# Revit family: VENTS-VKV
name_source: partatom
category: Mechanical Equipment
units: mm (PartAtom-declared; Revit-internal decimal feet)

## family parameters
Always vertical = Yes
Classification = None
Cut with Voids When Loaded = No
OmniClass Number = 23.75.35.17.14
OmniClass Title = Fans, Single Units
Part Type = Normal
Room Calculation Point = No
Round Connector Dimension = Use Diameter
Shared = No
Work Plane-Based = No

## types (38) — shared parameters
Casing Material = Fan Zinc
DboxFixDepth = 2 mm  [stored 0.00656168 ft]
DboxFixW = 80 mm  [stored 0.262467 ft]
Description = Centrifugal roof fan with vertical air discharge
Family Version = 1.0
Grid Material = Cover Grid Cross
Load Classification = HVAC
Maintenance Zone Front Depth = 400 mm
Maintenance Zone Material = Maintenance Zone
Maintenance Zone Side Depth = 400 mm
Manufacturer = Vents
Power Factor = 1
Protection rating = IP X4
URL = https://ventilation-system.com
zero-valued in all types: Sound Pressure Level at 1 m (dBA), Sound Pressure Level at 3 m (dBA)

## per-type parameters (varying)
- VKV 2E 190 (50Hz): A=417 mm; Af=155 mm; AswBottom=320 mm; B=355 mm; C=245 mm  [stored 0.803806 ft]; Current=0 A; D=213 mm  [stored 0.698819 ft]; DboxFixBottomH=40 mm  [stored 0.131234 ft]; DboxFixH=112 mm  [stored 0.367454 ft]; Duct Connection Size=180 mm  [stored 0.590551 ft]; H=170 mm  [stored 0.557743 ft]; Hb=36 mm  [stored 0.11811 ft]; Hc=82 mm  [stored 0.269029 ft]; Ht=52 mm  [stored 0.170604 ft]; L=480 mm; Maximum Air Flow=610 m³/h; Model=VKV 2E 190; Noise Level at 3 m (dBa)=48; Number of Poles=1; RPM (min-1)=2680; Transported Air Temperature (°C)=-25...+50; Type Comments=Centrifugal roof fan VKV 2E 190; Voltage=230 V; Weight=7.00 kg; gsA=334 mm
- VKV 2E 190 (60Hz): A=417 mm; Af=155 mm; AswBottom=320 mm; B=355 mm; C=245 mm  [stored 0.803806 ft]; Current=0 A; D=213 mm  [stored 0.698819 ft]; DboxFixBottomH=40 mm  [stored 0.131234 ft]; DboxFixH=112 mm  [stored 0.367454 ft]; Duct Connection Size=180 mm  [stored 0.590551 ft]; H=170 mm  [stored 0.557743 ft]; Hb=36 mm  [stored 0.11811 ft]; Hc=82 mm  [stored 0.269029 ft]; Ht=52 mm  [stored 0.170604 ft]; L=480 mm; Maximum Air Flow=654 m³/h; Model=VKV 2E 190; Noise Level at 3 m (dBa)=49; Number of Poles=1; RPM (min-1)=2980; Transported Air Temperature (°C)=-25...+50; Type Comments=Centrifugal roof fan VKV 2E 190; Voltage=230 V; Weight=7.00 kg; gsA=334 mm
- VKV 2E 220 (50Hz): A=417 mm; Af=155 mm; AswBottom=320 mm; B=355 mm; C=245 mm  [stored 0.803806 ft]; Current=0 A; D=213 mm  [stored 0.698819 ft]; DboxFixBottomH=40 mm  [stored 0.131234 ft]; DboxFixH=122 mm  [stored 0.400262 ft]; Duct Connection Size=180 mm  [stored 0.590551 ft]; H=190 mm; Hb=31 mm  [stored 0.101706 ft]; Hc=131 mm; Ht=28 mm  [stored 0.0918635 ft]; L=480 mm; Maximum Air Flow=880 m³/h; Model=VKV 2E 220; Noise Level at 3 m (dBa)=50; Number of Poles=1; RPM (min-1)=2580; Transported Air Temperature (°C)=-25...+50; Type Comments=Centrifugal roof fan VKV 2E 220; Voltage=230 V; Weight=7.00 kg; gsA=334 mm
- VKV 2E 220 (60Hz): A=417 mm; Af=155 mm; AswBottom=320 mm; B=355 mm; C=245 mm  [stored 0.803806 ft]; Current=1 A; D=213 mm  [stored 0.698819 ft]; DboxFixBottomH=40 mm  [stored 0.131234 ft]; DboxFixH=122 mm  [stored 0.400262 ft]; Duct Connection Size=180 mm  [stored 0.590551 ft]; H=190 mm; Hb=31 mm  [stored 0.101706 ft]; Hc=131 mm; Ht=28 mm  [stored 0.0918635 ft]; L=480 mm; Maximum Air Flow=883 m³/h; Model=VKV 2E 220; Noise Level at 3 m (dBa)=51; Number of Poles=1; RPM (min-1)=2840; Transported Air Temperature (°C)=-25...+50; Type Comments=Centrifugal roof fan VKV 2E 220; Voltage=230 V; Weight=7.00 kg; gsA=334 mm
- VKV 2E 225 (50Hz): A=417 mm; Af=155 mm; AswBottom=320 mm; B=355 mm; C=245 mm  [stored 0.803806 ft]; Current=1 A; D=210 mm  [stored 0.688976 ft]; DboxFixBottomH=40 mm  [stored 0.131234 ft]; DboxFixH=122 mm  [stored 0.400262 ft]; Duct Connection Size=180 mm  [stored 0.590551 ft]; H=215 mm; Hb=31 mm  [stored 0.101706 ft]; Hc=136 mm; Ht=48 mm  [stored 0.15748 ft]; L=480 mm; Maximum Air Flow=915 m³/h; Model=VKV 2E 225; Noise Level at 3 m (dBa)=51; Number of Poles=1; RPM (min-1)=2790; Transported Air Temperature (°C)=-25...+50; Type Comments=Centrifugal roof fan VKV 2E 225; Voltage=230 V; Weight=7.00 kg; gsA=334 mm
- VKV 2E 225 (60Hz): A=417 mm; Af=155 mm; AswBottom=320 mm; B=355 mm; C=245 mm  [stored 0.803806 ft]; Current=1 A; D=210 mm  [stored 0.688976 ft]; DboxFixBottomH=40 mm  [stored 0.131234 ft]; DboxFixH=122 mm  [stored 0.400262 ft]; Duct Connection Size=180 mm  [stored 0.590551 ft]; H=215 mm; Hb=31 mm  [stored 0.101706 ft]; Hc=136 mm; Ht=48 mm  [stored 0.15748 ft]; L=480 mm; Maximum Air Flow=1010 m³/h; Model=VKV 2E 225; Noise Level at 3 m (dBa)=52; Number of Poles=1; RPM (min-1)=2820; Transported Air Temperature (°C)=-25...+50; Type Comments=Centrifugal roof fan VKV 2E 225; Voltage=230 V; Weight=7.00 kg; gsA=334 mm
- VKV 4E 225 (50Hz): A=417 mm; Af=155 mm; AswBottom=320 mm; B=355 mm; C=245 mm  [stored 0.803806 ft]; Current=0 A; D=210 mm  [stored 0.688976 ft]; DboxFixBottomH=40 mm  [stored 0.131234 ft]; DboxFixH=122 mm  [stored 0.400262 ft]; Duct Connection Size=180 mm  [stored 0.590551 ft]; H=215 mm; Hb=31 mm  [stored 0.101706 ft]; Hc=136 mm; Ht=48 mm  [stored 0.15748 ft]; L=480 mm; Maximum Air Flow=738 m³/h; Model=VKV 4E 225; Noise Level at 3 m (dBa)=45; Number of Poles=1; RPM (min-1)=1400; Transported Air Temperature (°C)=-25...+50; Type Comments=Centrifugal roof fan VKV 4E 225; Voltage=230 V; Weight=7.00 kg; gsA=334 mm
- VKV 2E 250 (50Hz): A=481 mm; Af=179 mm; AswBottom=358 mm; B=425 mm; C=330 mm; Current=1 A; D=285 mm; DboxFixBottomH=36 mm  [stored 0.11811 ft]; DboxFixH=151 mm  [stored 0.495407 ft]; Duct Connection Size=250 mm; H=240 mm  [stored 0.787402 ft]; Hb=31 mm  [stored 0.101706 ft]; Hc=158 mm  [stored 0.518373 ft]; Ht=51 mm  [stored 0.167323 ft]; L=540 mm; Maximum Air Flow=1450 m³/h; Model=VKV 2E 250; Noise Level at 3 m (dBa)=54; Number of Poles=1; RPM (min-1)=2480; Transported Air Temperature (°C)=-25...+50; Type Comments=Centrifugal roof fan VKV 2E 250; Voltage=230 V; Weight=9.00 kg; gsA=385 mm
- VKV 2E 250 (60Hz): A=481 mm; Af=179 mm; AswBottom=358 mm; B=425 mm; C=330 mm; Current=1 A; D=285 mm; DboxFixBottomH=36 mm  [stored 0.11811 ft]; DboxFixH=151 mm  [stored 0.495407 ft]; Duct Connection Size=250 mm; H=240 mm  [stored 0.787402 ft]; Hb=31 mm  [stored 0.101706 ft]; Hc=158 mm  [stored 0.518373 ft]; Ht=51 mm  [stored 0.167323 ft]; L=540 mm; Maximum Air Flow=1320 m³/h; Model=VKV 2E 250; Noise Level at 3 m (dBa)=53; Number of Poles=1; RPM (min-1)=2320; Transported Air Temperature (°C)=-25...+50; Type Comments=Centrifugal roof fan VKV 2E 250; Voltage=230 V; Weight=9.00 kg; gsA=385 mm
- VKV 4E 250 (50Hz): A=481 mm; Af=179 mm; AswBottom=358 mm; B=425 mm; C=330 mm; Current=0 A; D=285 mm; DboxFixBottomH=36 mm  [stored 0.11811 ft]; DboxFixH=151 mm  [stored 0.495407 ft]; Duct Connection Size=250 mm; H=240 mm  [stored 0.787402 ft]; Hb=31 mm  [stored 0.101706 ft]; Hc=158 mm  [stored 0.518373 ft]; Ht=51 mm  [stored 0.167323 ft]; L=540 mm; Maximum Air Flow=820 m³/h; Model=VKV 4E 250; Noise Level at 3 m (dBa)=46; Number of Poles=1; RPM (min-1)=1440; Transported Air Temperature (°C)=-25...+50; Type Comments=Centrifugal roof fan VKV 4E 250; Voltage=230 V; Weight=9.00 kg; gsA=385 mm
- VKV 4E 280 (50Hz): A=547 mm; Af=204 mm; AswBottom=395 mm; B=425 mm; C=330 mm; Current=1 A; D=291 mm; DboxFixBottomH=53 mm  [stored 0.173885 ft]; DboxFixH=151 mm  [stored 0.495407 ft]; Duct Connection Size=250 mm; H=276 mm; Hb=31 mm  [stored 0.101706 ft]; Hc=194 mm  [stored 0.636483 ft]; Ht=51 mm  [stored 0.167323 ft]; L=600 mm; Maximum Air Flow=1490 m³/h; Model=VKV 4E 280; Noise Level at 3 m (dBa)=46; Number of Poles=1; RPM (min-1)=1446; Transported Air Temperature (°C)=-25...+50; Type Comments=Centrifugal roof fan VKV 4E 280; Voltage=230 V; Weight=13.00 kg; gsA=438 mm
- VKV 4E 280 (60Hz): A=547 mm; Af=204 mm; AswBottom=395 mm; B=425 mm; C=330 mm; Current=1 A; D=291 mm; DboxFixBottomH=53 mm  [stored 0.173885 ft]; DboxFixH=151 mm  [stored 0.495407 ft]; Duct Connection Size=250 mm; H=276 mm; Hb=31 mm  [stored 0.101706 ft]; Hc=194 mm  [stored 0.636483 ft]; Ht=51 mm  [stored 0.167323 ft]; L=600 mm; Maximum Air Flow=1520 m³/h; Model=VKV 4E 280; Noise Level at 3 m (dBa)=46; Number of Poles=1; RPM (min-1)=1710; Transported Air Temperature (°C)=-25...+50; Type Comments=Centrifugal roof fan VKV 4E 280; Voltage=230 V; Weight=13.00 kg; gsA=438 mm
- VKV 2E 310 (50Hz): A=613 mm; Af=229 mm; AswBottom=445 mm; B=477 mm; C=330 mm; Current=1 A; D=285 mm; DboxFixBottomH=75 mm; DboxFixH=151 mm  [stored 0.495407 ft]; Duct Connection Size=250 mm; H=300 mm; Hb=31 mm  [stored 0.101706 ft]; Hc=218 mm  [stored 0.715223 ft]; Ht=51 mm  [stored 0.167323 ft]; L=670 mm; Maximum Air Flow=2150 m³/h; Model=VKV 2E 310; Noise Level at 3 m (dBa)=58; Number of Poles=1; RPM (min-1)=2620; Transported Air Temperature (°C)=-25...+50; Type Comments=Centrifugal roof fan VKV 2E 310; Voltage=230 V; Weight=13.00 kg; gsA=490 mm
- VKV 4E 310 (50Hz): A=613 mm; Af=229 mm; AswBottom=445 mm; B=477 mm; C=330 mm; Current=1 A; D=285 mm; DboxFixBottomH=75 mm; DboxFixH=151 mm  [stored 0.495407 ft]; Duct Connection Size=250 mm; H=300 mm; Hb=31 mm  [stored 0.101706 ft]; Hc=218 mm  [stored 0.715223 ft]; Ht=51 mm  [stored 0.167323 ft]; L=670 mm; Maximum Air Flow=2265 m³/h; Model=VKV 4E 310; Noise Level at 3 m (dBa)=47; Number of Poles=1; RPM (min-1)=1420; Transported Air Temperature (°C)=-25...+50; Type Comments=Centrifugal roof fan VKV 4E 310; Voltage=230 V; Weight=20.00 kg; gsA=490 mm
- VKV 4E 310 (60Hz): A=613 mm; Af=229 mm; AswBottom=445 mm; B=477 mm; C=330 mm; Current=1 A; D=285 mm; DboxFixBottomH=75 mm; DboxFixH=151 mm  [stored 0.495407 ft]; Duct Connection Size=250 mm; H=300 mm; Hb=31 mm  [stored 0.101706 ft]; Hc=218 mm  [stored 0.715223 ft]; Ht=51 mm  [stored 0.167323 ft]; L=670 mm; Maximum Air Flow=2425 m³/h; Model=VKV 4E 310; Noise Level at 3 m (dBa)=49; Number of Poles=1; RPM (min-1)=1740; Transported Air Temperature (°C)=-25...+50; Type Comments=Centrifugal roof fan VKV 4E 310; Voltage=230 V; Weight=20.00 kg; gsA=490 mm
- VKV 4D 310 (50Hz): A=613 mm; Af=229 mm; AswBottom=445 mm; B=477 mm; C=750 mm; Current=0 A; D=285 mm; DboxFixBottomH=75 mm; DboxFixH=151 mm  [stored 0.495407 ft]; Duct Connection Size=250 mm; H=300 mm; Hb=31 mm  [stored 0.101706 ft]; Hc=218 mm  [stored 0.715223 ft]; Ht=51 mm  [stored 0.167323 ft]; L=670 mm; Maximum Air Flow=2300 m³/h; Model=VKV 4D 310; Noise Level at 3 m (dBa)=47; Number of Poles=3; RPM (min-1)=1410; Transported Air Temperature (°C)=-25...+50; Type Comments=Centrifugal roof fan VKV 4D 310; Voltage=400 V; Weight=19.00 kg; gsA=490 mm
- VKV 4D 310 (60Hz): A=613 mm; Af=229 mm; AswBottom=445 mm; B=477 mm; C=750 mm; Current=0 A; D=285 mm; DboxFixBottomH=75 mm; DboxFixH=151 mm  [stored 0.495407 ft]; Duct Connection Size=250 mm; H=300 mm; Hb=31 mm  [stored 0.101706 ft]; Hc=218 mm  [stored 0.715223 ft]; Ht=51 mm  [stored 0.167323 ft]; L=670 mm; Maximum Air Flow=2442 m³/h; Model=VKV 4D 310; Noise Level at 3 m (dBa)=48; Number of Poles=3; RPM (min-1)=1550; Transported Air Temperature (°C)=-25...+50; Type Comments=Centrifugal roof fan VKV 4D 310; Voltage=400 V; Weight=19.00 kg; gsA=490 mm
- VKV 4E 355 (50Hz): A=738 mm; Af=275 mm; AswBottom=546 mm; B=598 mm; C=450 mm; Current=1 A; D=438 mm; DboxFixBottomH=105 mm  [stored 0.344488 ft]; DboxFixH=151 mm  [stored 0.495407 ft]; Duct Connection Size=400 mm; H=330 mm; Hb=31 mm  [stored 0.101706 ft]; Hc=248 mm; Ht=51 mm  [stored 0.167323 ft]; L=790 mm; Maximum Air Flow=2480 m³/h; Model=VKV 4E 355; Noise Level at 3 m (dBa)=51; Number of Poles=1; RPM (min-1)=1420; Transported Air Temperature (°C)=-30...+60; Type Comments=Centrifugal roof fan VKV 4E 355; Voltage=230 V; Weight=26.00 kg; gsA=590 mm
- VKV 4E 355 (60Hz): A=738 mm; Af=275 mm; AswBottom=546 mm; B=598 mm; C=450 mm; Current=1 A; D=438 mm; DboxFixBottomH=105 mm  [stored 0.344488 ft]; DboxFixH=151 mm  [stored 0.495407 ft]; Duct Connection Size=400 mm; H=330 mm; Hb=31 mm  [stored 0.101706 ft]; Hc=248 mm; Ht=51 mm  [stored 0.167323 ft]; L=790 mm; Maximum Air Flow=2976 m³/h; Model=VKV 4E 355; Noise Level at 3 m (dBa)=52; Number of Poles=1; RPM (min-1)=1580; Transported Air Temperature (°C)=-30...+60; Type Comments=Centrifugal roof fan VKV 4E 355; Voltage=230 V; Weight=26.00 kg; gsA=590 mm
- VKV 4D 355 (50Hz): A=738 mm; Af=275 mm; AswBottom=546 mm; B=598 mm; C=450 mm; Current=1 A; D=438 mm; DboxFixBottomH=105 mm  [stored 0.344488 ft]; DboxFixH=151 mm  [stored 0.495407 ft]; Duct Connection Size=400 mm; H=330 mm; Hb=31 mm  [stored 0.101706 ft]; Hc=248 mm; Ht=51 mm  [stored 0.167323 ft]; L=790 mm; Maximum Air Flow=3290 m³/h; Model=VKV 4D 355; Noise Level at 3 m (dBa)=52; Number of Poles=3; RPM (min-1)=1430; Transported Air Temperature (°C)=-30...+60; Type Comments=Centrifugal roof fan VKV 4D 355; Voltage=400 V; Weight=26.00 kg; gsA=590 mm
- VKV 4D 355 (60Hz): A=738 mm; Af=275 mm; AswBottom=546 mm; B=598 mm; C=450 mm; Current=1 A; D=438 mm; DboxFixBottomH=105 mm  [stored 0.344488 ft]; DboxFixH=151 mm  [stored 0.495407 ft]; Duct Connection Size=400 mm; H=330 mm; Hb=31 mm  [stored 0.101706 ft]; Hc=248 mm; Ht=51 mm  [stored 0.167323 ft]; L=790 mm; Maximum Air Flow=3540 m³/h; Model=VKV 4D 355; Noise Level at 3 m (dBa)=53; Number of Poles=3; RPM (min-1)=1650; Transported Air Temperature (°C)=-30...+60; Type Comments=Centrifugal roof fan VKV 4D 355; Voltage=400 V; Weight=26.00 kg; gsA=590 mm
- VKV 4E 400 (50Hz): A=738 mm; Af=275 mm; AswBottom=562 mm; B=598 mm; C=450 mm; Current=2 A; D=438 mm; DboxFixBottomH=82 mm  [stored 0.269029 ft]; DboxFixH=151 mm  [stored 0.495407 ft]; Duct Connection Size=400 mm; H=375 mm; Hb=31 mm  [stored 0.101706 ft]; Hc=224 mm; Ht=120 mm  [stored 0.393701 ft]; L=790 mm; Maximum Air Flow=3950 m³/h; Model=VKV 4E 400; Noise Level at 3 m (dBa)=55; Number of Poles=1; RPM (min-1)=1440; Transported Air Temperature (°C)=-30...+60; Type Comments=Centrifugal roof fan VKV 4E 400; Voltage=230 V; Weight=33.00 kg; gsA=590 mm
- VKV 6E 400 (50Hz): A=738 mm; Af=275 mm; AswBottom=562 mm; B=598 mm; C=450 mm; Current=1 A; D=438 mm; DboxFixBottomH=82 mm  [stored 0.269029 ft]; DboxFixH=151 mm  [stored 0.495407 ft]; Duct Connection Size=400 mm; H=375 mm; Hb=31 mm  [stored 0.101706 ft]; Hc=224 mm; Ht=120 mm  [stored 0.393701 ft]; L=790 mm; Maximum Air Flow=2740 m³/h; Model=VKV 6E 400; Noise Level at 3 m (dBa)=47; Number of Poles=1; RPM (min-1)=945; Transported Air Temperature (°C)=-30...+60; Type Comments=Centrifugal roof fan VKV 6E 400; Voltage=230 V; Weight=31.00 kg; gsA=590 mm
- VKV 6E 400 (60Hz): A=738 mm; Af=275 mm; AswBottom=562 mm; B=598 mm; C=450 mm; Current=1 A; D=438 mm; DboxFixBottomH=82 mm  [stored 0.269029 ft]; DboxFixH=151 mm  [stored 0.495407 ft]; Duct Connection Size=400 mm; H=375 mm; Hb=31 mm  [stored 0.101706 ft]; Hc=224 mm; Ht=120 mm  [stored 0.393701 ft]; L=790 mm; Maximum Air Flow=3289 m³/h; Model=VKV 6E 400; Noise Level at 3 m (dBa)=49; Number of Poles=1; RPM (min-1)=1071; Transported Air Temperature (°C)=-30...+60; Type Comments=Centrifugal roof fan VKV 6E 400; Voltage=230 V; Weight=31.00 kg; gsA=590 mm
- VKV 4D 400 (50Hz): A=738 mm; Af=275 mm; AswBottom=562 mm; B=598 mm; C=450 mm; Current=1 A; D=438 mm; DboxFixBottomH=82 mm  [stored 0.269029 ft]; DboxFixH=151 mm  [stored 0.495407 ft]; Duct Connection Size=400 mm; H=375 mm; Hb=31 mm  [stored 0.101706 ft]; Hc=224 mm; Ht=120 mm  [stored 0.393701 ft]; L=790 mm; Maximum Air Flow=3950 m³/h; Model=VKV 4D 400; Noise Level at 3 m (dBa)=55; Number of Poles=3; RPM (min-1)=1440; Transported Air Temperature (°C)=-30...+60; Type Comments=Centrifugal roof fan VKV 4D 400; Voltage=400 V; Weight=33.00 kg; gsA=590 mm
- VKV 4E 450 (50Hz): A=738 mm; Af=275 mm; AswBottom=546 mm; B=668 mm; C=535 mm; Current=3 A; D=438 mm; DboxFixBottomH=154 mm  [stored 0.505249 ft]; DboxFixH=151 mm  [stored 0.495407 ft]; Duct Connection Size=400 mm; H=430 mm; Hb=31 mm  [stored 0.101706 ft]; Hc=309 mm; Ht=90 mm  [stored 0.295276 ft]; L=790 mm; Maximum Air Flow=6180 m³/h; Model=VKV 4E 450; Noise Level at 3 m (dBa)=58; Number of Poles=1; RPM (min-1)=1400; Transported Air Temperature (°C)=-30...+60; Type Comments=Centrifugal roof fan VKV 4E 450; Voltage=230 V; Weight=41.00 kg; gsA=590 mm
- VKV 6E 450 (50Hz): A=738 mm; Af=275 mm; AswBottom=546 mm; B=668 mm; C=535 mm; Current=1 A; D=438 mm; DboxFixBottomH=154 mm  [stored 0.505249 ft]; DboxFixH=151 mm  [stored 0.495407 ft]; Duct Connection Size=400 mm; H=430 mm; Hb=31 mm  [stored 0.101706 ft]; Hc=309 mm; Ht=90 mm  [stored 0.295276 ft]; L=790 mm; Maximum Air Flow=4380 m³/h; Model=VKV 6E 450; Noise Level at 3 m (dBa)=50; Number of Poles=1; RPM (min-1)=940; Transported Air Temperature (°C)=-30...+60; Type Comments=Centrifugal roof fan VKV 6E 450; Voltage=230 V; Weight=41.00 kg; gsA=590 mm
- VKV 4D 450 (50Hz): A=738 mm; Af=275 mm; AswBottom=546 mm; B=668 mm; C=535 mm; Current=2 A; D=438 mm; DboxFixBottomH=154 mm  [stored 0.505249 ft]; DboxFixH=151 mm  [stored 0.495407 ft]; Duct Connection Size=400 mm; H=425 mm; Hb=31 mm  [stored 0.101706 ft]; Hc=304 mm; Ht=90 mm  [stored 0.295276 ft]; L=790 mm; Maximum Air Flow=5920 m³/h; Model=VKV 4D 450; Noise Level at 3 m (dBa)=57; Number of Poles=3; RPM (min-1)=1440; Transported Air Temperature (°C)=-30...+50; Type Comments=Centrifugal roof fan VKV 4D 450; Voltage=400 V; Weight=41.00 kg; gsA=590 mm
- VKV 4D 500 (50Hz): A=859 mm; Af=320 mm; AswBottom=594 mm; B=668 mm; C=535 mm; Current=3 A; D=430 mm; DboxFixBottomH=198 mm  [stored 0.649606 ft]; DboxFixH=151 mm  [stored 0.495407 ft]; Duct Connection Size=400 mm; H=460 mm; Hb=31 mm  [stored 0.101706 ft]; Hc=339 mm; Ht=90 mm  [stored 0.295276 ft]; L=910 mm; Maximum Air Flow=8435 m³/h; Model=VKV 4D 500; Noise Level at 3 m (dBa)=62; Number of Poles=3; RPM (min-1)=1460; Transported Air Temperature (°C)=-30...+50; Type Comments=Centrifugal roof fan VKV 4D 500; Voltage=400 V; Weight=52.00 kg; gsA=687 mm
- VKV 6E 500 (50Hz): A=859 mm; Af=320 mm; AswBottom=594 mm; B=668 mm; C=535 mm; Current=2 A; D=445 mm; DboxFixBottomH=198 mm  [stored 0.649606 ft]; DboxFixH=151 mm  [stored 0.495407 ft]; Duct Connection Size=400 mm; H=460 mm; Hb=31 mm  [stored 0.101706 ft]; Hc=339 mm; Ht=90 mm  [stored 0.295276 ft]; L=910 mm; Maximum Air Flow=5680 m³/h; Model=VKV 6E 500; Noise Level at 3 m (dBa)=52; Number of Poles=1; RPM (min-1)=970; Transported Air Temperature (°C)=-25...+60; Type Comments=Centrifugal roof fan VKV 6E 500; Voltage=230 V; Weight=52.00 kg; gsA=687 mm
- VKV 6E 500 (60Hz): A=859 mm; Af=320 mm; AswBottom=594 mm; B=668 mm; C=535 mm; Current=3 A; D=445 mm; DboxFixBottomH=198 mm  [stored 0.649606 ft]; DboxFixH=151 mm  [stored 0.495407 ft]; Duct Connection Size=400 mm; H=460 mm; Hb=31 mm  [stored 0.101706 ft]; Hc=339 mm; Ht=90 mm  [stored 0.295276 ft]; L=910 mm; Maximum Air Flow=6532 m³/h; Model=VKV 6E 500; Noise Level at 3 m (dBa)=54; Number of Poles=1; RPM (min-1)=1120; Transported Air Temperature (°C)=-25...+60; Type Comments=Centrifugal roof fan VKV 6E 500; Voltage=230 V; Weight=52.00 kg; gsA=687 mm
- VKV 6D 500 (50Hz): A=859 mm; Af=320 mm; AswBottom=594 mm; B=668 mm; C=535 mm; Current=1 A; D=445 mm; DboxFixBottomH=198 mm  [stored 0.649606 ft]; DboxFixH=151 mm  [stored 0.495407 ft]; Duct Connection Size=400 mm; H=460 mm; Hb=31 mm  [stored 0.101706 ft]; Hc=339 mm; Ht=90 mm  [stored 0.295276 ft]; L=910 mm; Maximum Air Flow=6000 m³/h; Model=VKV 6D 500; Noise Level at 3 m (dBa)=52; Number of Poles=3; RPM (min-1)=978; Transported Air Temperature (°C)=-25...+60; Type Comments=Centrifugal roof fan VKV 6D 500; Voltage=400 V; Weight=52.00 kg; gsA=687 mm
- VKV 6D 500 (60Hz): A=859 mm; Af=320 mm; AswBottom=594 mm; B=668 mm; C=535 mm; Current=1 A; D=445 mm; DboxFixBottomH=198 mm  [stored 0.649606 ft]; DboxFixH=151 mm  [stored 0.495407 ft]; Duct Connection Size=400 mm; H=460 mm; Hb=31 mm  [stored 0.101706 ft]; Hc=339 mm; Ht=90 mm  [stored 0.295276 ft]; L=910 mm; Maximum Air Flow=6122 m³/h; Model=VKV 6D 500; Noise Level at 3 m (dBa)=54; Number of Poles=3; RPM (min-1)=1125; Transported Air Temperature (°C)=-25...+60; Type Comments=Centrifugal roof fan VKV 6D 500; Voltage=400 V; Weight=52.00 kg; gsA=687 mm
- VKV 4D 560 (50Hz): A=859 mm; Af=320 mm; AswBottom=722 mm; B=833 mm; C=750 mm; Current=3 A; D=605 mm; DboxFixBottomH=150 mm; DboxFixH=151 mm  [stored 0.495407 ft]; Duct Connection Size=560 mm; H=485 mm; Hb=31 mm  [stored 0.101706 ft]; Hc=342 mm; Ht=112 mm  [stored 0.367454 ft]; L=910 mm; Maximum Air Flow=13560 m³/h; Model=VKV 4D 560; Noise Level at 3 m (dBa)=66; Number of Poles=1; RPM (min-1)=1400; Transported Air Temperature (°C)=-25...+50; Type Comments=Centrifugal roof fan VKV 4D 560; Voltage=230 V; Weight=63.00 kg; gsA=687 mm
- VKV 6E 560 (50Hz): A=859 mm; Af=320 mm; AswBottom=722 mm; B=833 mm; C=750 mm; Current=3 A; D=605 mm; DboxFixBottomH=150 mm; DboxFixH=151 mm  [stored 0.495407 ft]; Duct Connection Size=560 mm; H=485 mm; Hb=31 mm  [stored 0.101706 ft]; Hc=342 mm; Ht=112 mm  [stored 0.367454 ft]; L=910 mm; Maximum Air Flow=9560 m³/h; Model=VKV 6E 560; Noise Level at 3 m (dBa)=58; Number of Poles=1; RPM (min-1)=930; Transported Air Temperature (°C)=-25...+50; Type Comments=Centrifugal roof fan VKV 6E 560; Voltage=230 V; Weight=63.00 kg; gsA=687 mm
- VKV 6D 560 (50Hz): A=859 mm; Af=320 mm; AswBottom=722 mm; B=833 mm; C=750 mm; Current=1 A; D=605 mm; DboxFixBottomH=150 mm; DboxFixH=151 mm  [stored 0.495407 ft]; Duct Connection Size=560 mm; H=485 mm; Hb=31 mm  [stored 0.101706 ft]; Hc=342 mm; Ht=112 mm  [stored 0.367454 ft]; L=910 mm; Maximum Air Flow=9630 m³/h; Model=VKV 6D 560; Noise Level at 3 m (dBa)=58; Number of Poles=3; RPM (min-1)=970; Transported Air Temperature (°C)=-25...+50; Type Comments=Centrifugal roof fan VKV 6D 560; Voltage=400 V; Weight=63.00 kg; gsA=687 mm
- VKV 6D 630 (50Hz): A=951 mm; Af=355 mm; AswBottom=782 mm; B=939 mm; C=750 mm; Current=2 A; D=600 mm; DboxFixBottomH=186 mm  [stored 0.610236 ft]; DboxFixH=151 mm  [stored 0.495407 ft]; Duct Connection Size=560 mm; H=485 mm; Hb=36 mm  [stored 0.11811 ft]; Hc=337 mm; Ht=112 mm  [stored 0.367454 ft]; L=1000 mm; Maximum Air Flow=12640 m³/h; Model=VKV 6D 630; Noise Level at 3 m (dBa)=64; Number of Poles=3; RPM (min-1)=957; Transported Air Temperature (°C)=-25...+50; Type Comments=Centrifugal roof fan VKV 6D 630; Voltage=400 V; Weight=81.00 kg; gsA=761 mm
- VKV 6D 710 (50Hz): A=992 mm; Af=370 mm; AswBottom=820 mm; B=980 mm; C=840 mm; Current=5 A; D=674 mm; DboxFixBottomH=186 mm  [stored 0.610236 ft]; DboxFixH=151 mm  [stored 0.495407 ft]; Duct Connection Size=630 mm; H=485 mm; Hb=36 mm  [stored 0.11811 ft]; Hc=313 mm; Ht=136 mm; L=1040 mm; Maximum Air Flow=17010 m³/h; Model=VKV 6D 710; Noise Level at 3 m (dBa)=67; Number of Poles=3; RPM (min-1)=945; Transported Air Temperature (°C)=-25...+70; Type Comments=Centrifugal roof fan VKV 6D 710; Voltage=400 V; Weight=114.00 kg; gsA=794 mm

note: [stored X ft] marks values corroborated as IEEE doubles in the binary element streams (Revit-internal decimal feet)

## geometry (parser evidence)
native form markers: Sweep x8
no freeform markers — native parametric forms only
